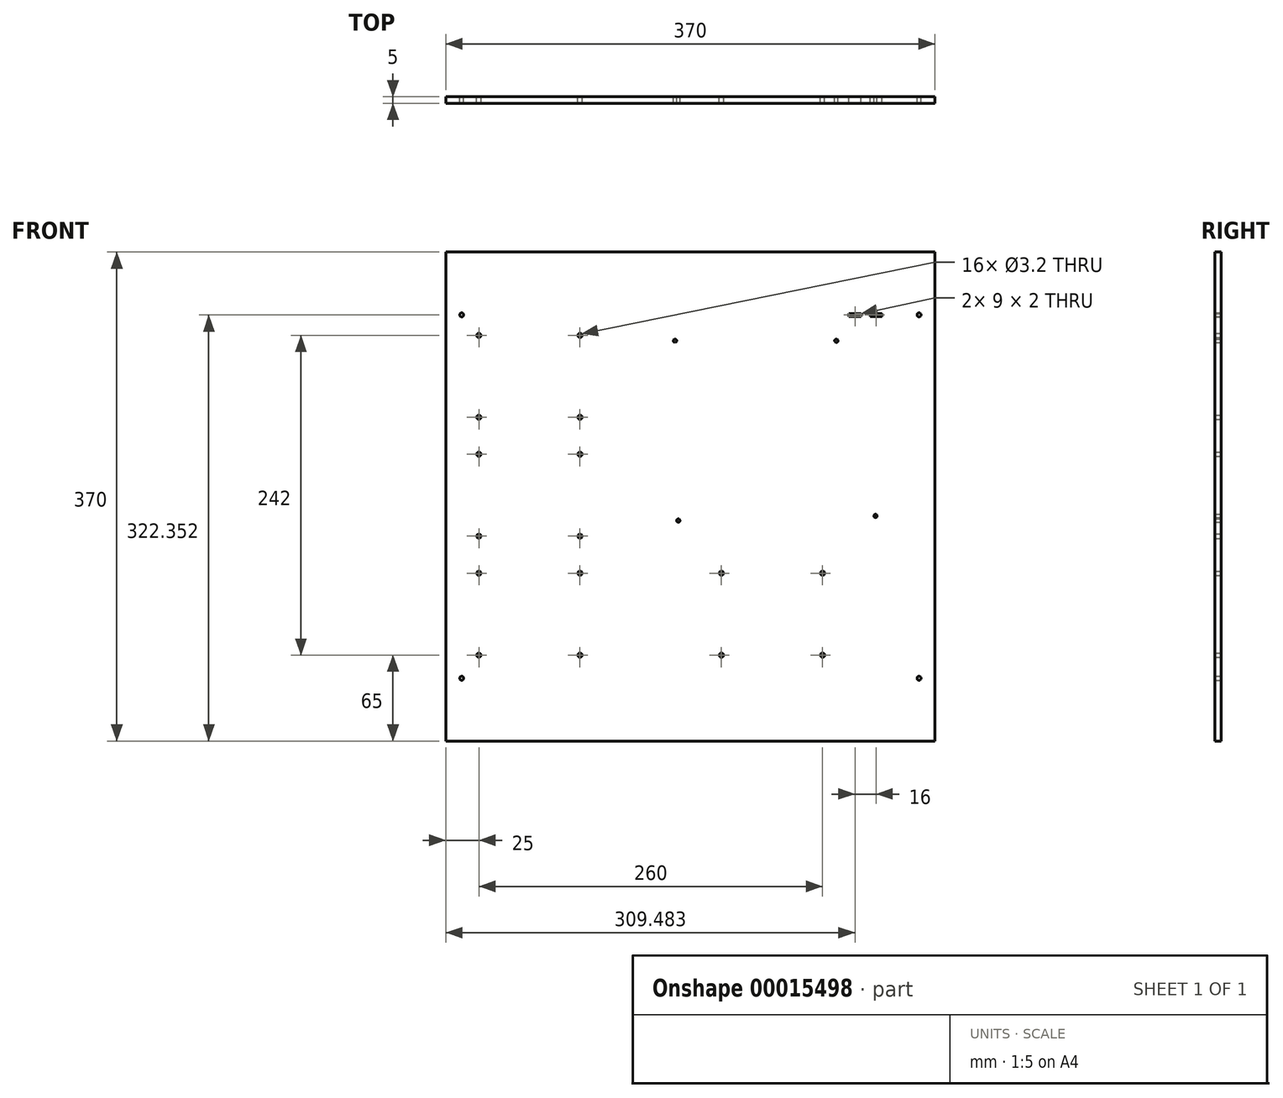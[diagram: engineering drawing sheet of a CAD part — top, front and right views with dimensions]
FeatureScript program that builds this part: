
annotation { "Feature Type Name" : "Feature", "Feature Type Description" : "" }
export const myFeature = defineFeature(function(context is Context, id is Id, definition is map)
    precondition{}
    {
        {
            var Q0;
            Q0=qCreatedBy(makeId("Front.planeOp"),FACE);
            var sketch = newSketch(context, id + "F0", { "sketchPlane" : qUnion([Q0])});
            skLineSegment(sketch, "E0.rect.bottom", {"start": v(185, 185) * mm, "end": v(-185, 185) * mm});
            skLineSegment(sketch, "E0.rect.top", {"start": v(185, -185) * mm, "end": v(-185, -185) * mm});
            skLineSegment(sketch, "E0.rect.left", {"start": v(185, 185) * mm, "end": v(185, -185) * mm});
            skLineSegment(sketch, "E0.rect.right", {"start": v(-185, 185) * mm, "end": v(-185, -185) * mm});
            skPoint(sketch, "E0.rect.middle", {"position": v(0, 0) * mm});
            skSolve(sketch);
        }
        {
            var Q0;
            Q0=qSketchRegion(id+"F0",true);
            extrude(context, id + "F1", {"entities" : qUnion([Q0]), "depth" : 5 * mm});
        }
        {
            var Q0;
            Q0=qCreatedBy(makeId("Front.planeOp"),FACE);
            var sketch = newSketch(context, id + "F2", { "sketchPlane" : qUnion([Q0])});
            skCircle(sketch, "E1", {"center": v(-173, 137.5) * mm, "radius": 1.5 * mm});
            skLineSegment(sketch, "E2.rect.bottom", {"start": v(-173, 137.5) * mm, "end": v(173, 137.5) * mm, "construction": true});
            skLineSegment(sketch, "E2.rect.top", {"start": v(-173, -137.5) * mm, "end": v(173, -137.5) * mm, "construction": true});
            skLineSegment(sketch, "E2.rect.left", {"start": v(-173, 137.5) * mm, "end": v(-173, -137.5) * mm, "construction": true});
            skLineSegment(sketch, "E2.rect.right", {"start": v(173, 137.5) * mm, "end": v(173, -137.5) * mm, "construction": true});
            skPoint(sketch, "E2.rect.middle", {"position": v(0, 0) * mm});
            skCircle(sketch, "E3", {"center": v(173, 137.5) * mm, "radius": 1.5 * mm});
            skCircle(sketch, "E4", {"center": v(173, -137.5) * mm, "radius": 1.5 * mm});
            skCircle(sketch, "E5", {"center": v(-173, -137.5) * mm, "radius": 1.5 * mm});
            skSolve(sketch);
        }
        {
            var Q0;
            Q0=qSketchRegion(id+"F2",true);
            extrude(context, id + "F3", {"entities" : qUnion([Q0]), "operationType" : NewBodyOperationType.REMOVE, "endBound" : BoundingType.THROUGH_ALL, "depth" : 25 * mm});
        }
        {
            var Q0;
            Q0=qCreatedBy(makeId("Front.planeOp"),FACE);
            var sketch = newSketch(context, id + "F4", { "sketchPlane" : qUnion([Q0])});
            skLineSegment(sketch, "E6.bottom", {"start": v(119.98, 138.35) * mm, "end": v(128.98, 138.35) * mm});
            skLineSegment(sketch, "E6.top", {"start": v(119.98, 136.35) * mm, "end": v(128.98, 136.35) * mm});
            skLineSegment(sketch, "E6.left", {"start": v(119.98, 138.35) * mm, "end": v(119.98, 136.35) * mm});
            skLineSegment(sketch, "E6.right", {"start": v(128.98, 138.35) * mm, "end": v(128.98, 136.35) * mm});
            skLineSegment(sketch, "E7.bottom", {"start": v(135.98, 138.35) * mm, "end": v(144.98, 138.35) * mm});
            skLineSegment(sketch, "E7.top", {"start": v(135.98, 136.35) * mm, "end": v(144.98, 136.35) * mm});
            skLineSegment(sketch, "E7.left", {"start": v(135.98, 138.35) * mm, "end": v(135.98, 136.35) * mm});
            skLineSegment(sketch, "E7.right", {"start": v(144.98, 138.35) * mm, "end": v(144.98, 136.35) * mm});
            skSolve(sketch);
        }
        {
            var Q0;
            Q0 = qSketchRegion(id + "F4", true);
            extrude(context, id + "F5", {"entities" : qUnion([Q0]), "operationType" : NewBodyOperationType.REMOVE, "endBound" : BoundingType.UP_TO_NEXT, "depth" : 25 * mm});
        }
        {
            var Q0;
            Q0=qCreatedBy(makeId("Front.planeOp"),FACE);
            var sketch = newSketch(context, id + "F6", { "sketchPlane" : qUnion([Q0])});
            skPoint(sketch, "E8", {"position": v(-11.58, 117.9) * mm});
            skPoint(sketch, "E9", {"position": v(110.43, 117.9) * mm});
            skPoint(sketch, "E10", {"position": v(140.05, -14.69) * mm});
            skPoint(sketch, "E11", {"position": v(-9.11, -18.21) * mm});
            skSolve(sketch);
        }
        {
            var Q0;
            Q0=sQuery(id+"F6.wireOp",VERTEX,"E8");
            var Q1;
            Q1=sQuery(id+"F6.wireOp",VERTEX,"E11");
            var Q2;
            Q2=sQuery(id+"F6.wireOp",VERTEX,"E10");
            var Q3;
            Q3=sQuery(id+"F6.wireOp",VERTEX,"E9");
            var Q4;
            Q4=makeQuery(id+"F1.opExtrude","SWEPT_BODY",BODY,{"disambiguationData":[OSD([sQuery(id+"F0.wireOp",EDGE,"E0.rect.bottom"),sQuery(id+"F0.wireOp",EDGE,"E0.rect.top"),sQuery(id+"F0.wireOp",EDGE,"E0.rect.left"),sQuery(id+"F0.wireOp",EDGE,"E0.rect.right")])]});
            hole(context, id + "F7", {"style" : HoleStyle.SIMPLE, "holeDiameter" : 2.5 * mm, "endStyle" : HoleEndStyle.THROUGH, "oppositeDirection" : true, "locations" : qUnion([Q0, Q1, Q2, Q3]), "scope" : qUnion([Q4])});
        }
        {
            var Q0;
            Q0=qCreatedBy(makeId("Front.planeOp"),FACE);
            var sketch = newSketch(context, id + "F8", { "sketchPlane" : qUnion([Q0])});
            skLineSegment(sketch, "E12.bottom", {"start": v(-160, -58) * mm, "end": v(-83.5, -58) * mm, "construction": true});
            skLineSegment(sketch, "E12.top", {"start": v(-160, -120) * mm, "end": v(-83.5, -120) * mm, "construction": true});
            skLineSegment(sketch, "E12.left", {"start": v(-160, -58) * mm, "end": v(-160, -120) * mm, "construction": true});
            skLineSegment(sketch, "E12.right", {"start": v(-83.5, -58) * mm, "end": v(-83.5, -120) * mm, "construction": true});
            skLineSegment(sketch, "E13.bottom", {"start": v(23.5, -58) * mm, "end": v(100, -58) * mm, "construction": true});
            skLineSegment(sketch, "E13.top", {"start": v(23.5, -120) * mm, "end": v(100, -120) * mm, "construction": true});
            skLineSegment(sketch, "E13.left", {"start": v(23.5, -58) * mm, "end": v(23.5, -120) * mm, "construction": true});
            skLineSegment(sketch, "E13.right", {"start": v(100, -58) * mm, "end": v(100, -120) * mm, "construction": true});
            skPoint(sketch, "E14", {"position": v(-160, -58) * mm});
            skPoint(sketch, "E15", {"position": v(-160, -120) * mm});
            skPoint(sketch, "E16", {"position": v(-83.5, -120) * mm});
            skPoint(sketch, "E17", {"position": v(-83.5, -58) * mm});
            skPoint(sketch, "E18", {"position": v(23.5, -58) * mm});
            skPoint(sketch, "E19", {"position": v(23.5, -120) * mm});
            skPoint(sketch, "E20", {"position": v(100, -120) * mm});
            skPoint(sketch, "E21", {"position": v(100, -58) * mm});
            skSolve(sketch);
        }
        {
            var Q0;
            Q0=sQuery(id+"F8.wireOp",VERTEX,"E15");
            var Q1;
            Q1=sQuery(id+"F8.wireOp",VERTEX,"E14");
            var Q2;
            Q2=sQuery(id+"F8.wireOp",VERTEX,"E17");
            var Q3;
            Q3=sQuery(id+"F8.wireOp",VERTEX,"E16");
            var Q4;
            Q4=sQuery(id+"F8.wireOp",VERTEX,"E19");
            var Q5;
            Q5=sQuery(id+"F8.wireOp",VERTEX,"E18");
            var Q6;
            Q6=sQuery(id+"F8.wireOp",VERTEX,"E21");
            var Q7;
            Q7=sQuery(id+"F8.wireOp",VERTEX,"E20");
            var Q8;
            Q8=makeQuery(id+"F1.opExtrude","SWEPT_BODY",BODY,{"disambiguationData":[OSD([sQuery(id+"F0.wireOp",EDGE,"E0.rect.bottom"),sQuery(id+"F0.wireOp",EDGE,"E0.rect.top"),sQuery(id+"F0.wireOp",EDGE,"E0.rect.left"),sQuery(id+"F0.wireOp",EDGE,"E0.rect.right")])]});
            hole(context, id + "F9", {"style" : HoleStyle.SIMPLE, "holeDiameter" : 3.2 * mm, "endStyle" : HoleEndStyle.THROUGH, "oppositeDirection" : true, "locations" : qUnion([Q0, Q1, Q2, Q3, Q4, Q5, Q6, Q7]), "scope" : qUnion([Q8])});
        }
        {
            var Q0;
            Q0=qCreatedBy(makeId("Front.planeOp"),FACE);
            var sketch = newSketch(context, id + "F10", { "sketchPlane" : qUnion([Q0])});
            skLineSegment(sketch, "E22.bottom", {"start": v(-160, 122) * mm, "end": v(-83.5, 122) * mm, "construction": true});
            skLineSegment(sketch, "E22.top", {"start": v(-160, 60) * mm, "end": v(-83.5, 60) * mm, "construction": true});
            skLineSegment(sketch, "E22.left", {"start": v(-160, 122) * mm, "end": v(-160, 60) * mm, "construction": true});
            skLineSegment(sketch, "E22.right", {"start": v(-83.5, 122) * mm, "end": v(-83.5, 60) * mm, "construction": true});
            skLineSegment(sketch, "E23.bottom", {"start": v(-160, 32) * mm, "end": v(-83.5, 32) * mm, "construction": true});
            skLineSegment(sketch, "E23.top", {"start": v(-160, -30) * mm, "end": v(-83.5, -30) * mm, "construction": true});
            skLineSegment(sketch, "E23.left", {"start": v(-160, 32) * mm, "end": v(-160, -30) * mm, "construction": true});
            skLineSegment(sketch, "E23.right", {"start": v(-83.5, 32) * mm, "end": v(-83.5, -30) * mm, "construction": true});
            skPoint(sketch, "E24", {"position": v(-160, 122) * mm});
            skPoint(sketch, "E25", {"position": v(-160, 60) * mm});
            skPoint(sketch, "E26", {"position": v(-160, 32) * mm});
            skPoint(sketch, "E27", {"position": v(-160, -30) * mm});
            skPoint(sketch, "E28", {"position": v(-83.5, -30) * mm});
            skPoint(sketch, "E29", {"position": v(-83.5, 32) * mm});
            skPoint(sketch, "E30", {"position": v(-83.5, 60) * mm});
            skPoint(sketch, "E31", {"position": v(-83.5, 122) * mm});
            skSolve(sketch);
        }
        {
            var Q0;
            Q0=sQuery(id+"F10.wireOp",VERTEX,"E25");
            var Q1;
            Q1=sQuery(id+"F10.wireOp",VERTEX,"E26");
            var Q2;
            Q2=sQuery(id+"F10.wireOp",VERTEX,"E27");
            var Q3;
            Q3=sQuery(id+"F10.wireOp",VERTEX,"E28");
            var Q4;
            Q4=sQuery(id+"F10.wireOp",VERTEX,"E29");
            var Q5;
            Q5=sQuery(id+"F10.wireOp",VERTEX,"E30");
            var Q6;
            Q6=sQuery(id+"F10.wireOp",VERTEX,"E31");
            var Q7;
            Q7=sQuery(id+"F10.wireOp",VERTEX,"E24");
            var Q8;
            Q8=makeQuery(id+"F1.opExtrude","SWEPT_BODY",BODY,{"disambiguationData":[OSD([sQuery(id+"F0.wireOp",EDGE,"E0.rect.bottom"),sQuery(id+"F0.wireOp",EDGE,"E0.rect.top"),sQuery(id+"F0.wireOp",EDGE,"E0.rect.left"),sQuery(id+"F0.wireOp",EDGE,"E0.rect.right")])]});
            hole(context, id + "F11", {"style" : HoleStyle.SIMPLE, "holeDiameter" : 3.2 * mm, "endStyle" : HoleEndStyle.THROUGH, "oppositeDirection" : true, "locations" : qUnion([Q0, Q1, Q2, Q3, Q4, Q5, Q6, Q7]), "scope" : qUnion([Q8])});
        }
    });
